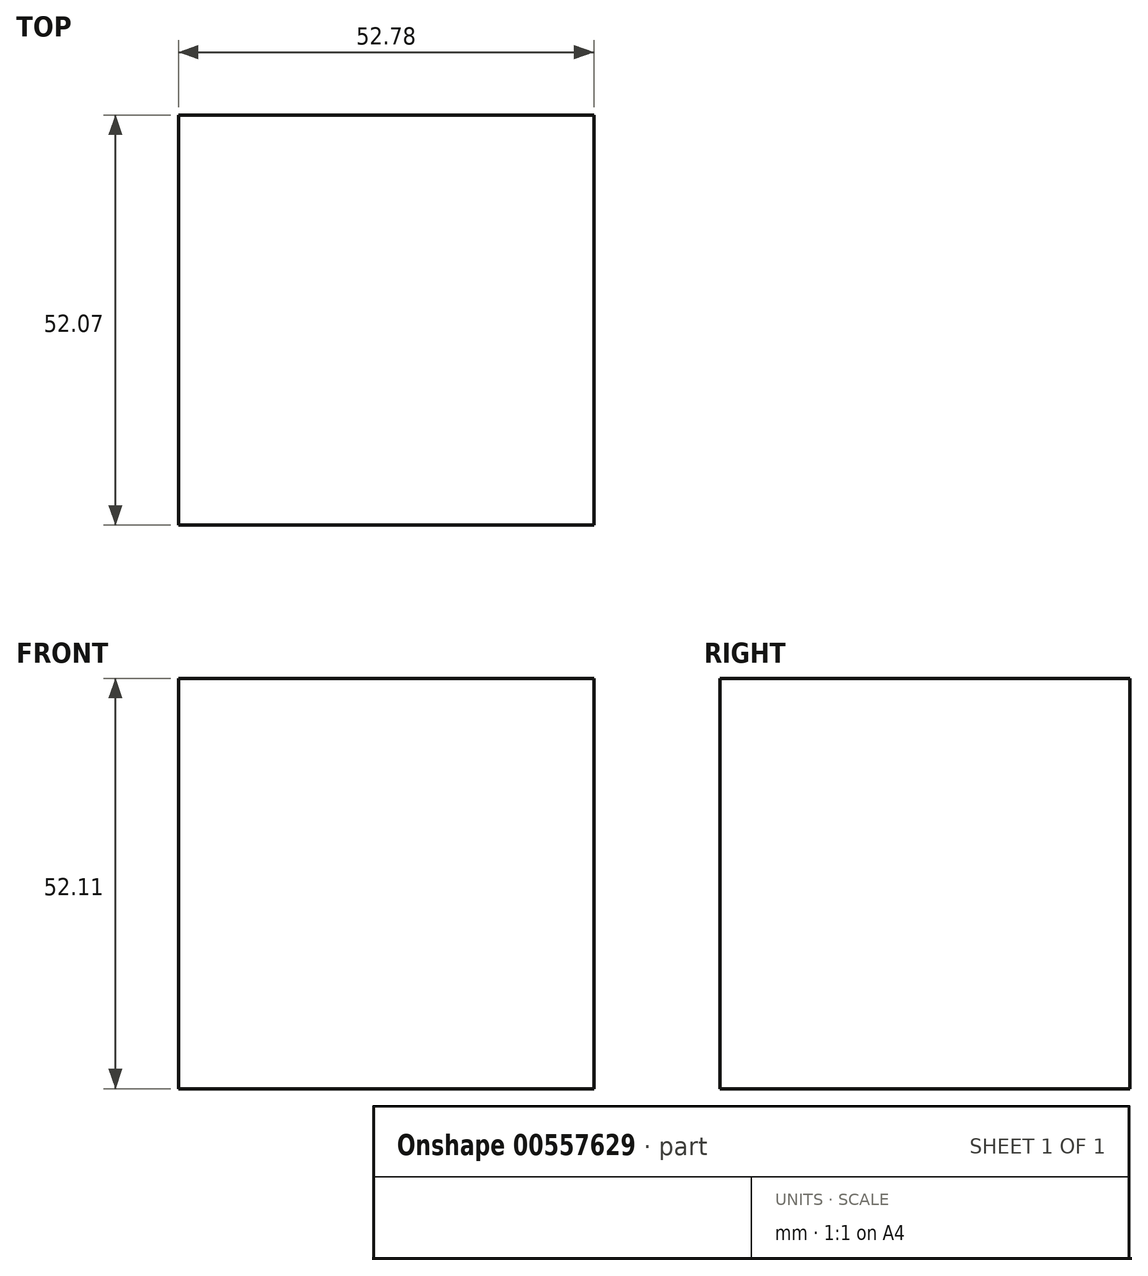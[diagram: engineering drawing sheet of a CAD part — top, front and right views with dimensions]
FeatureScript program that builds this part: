
annotation { "Feature Type Name" : "Feature", "Feature Type Description" : "" }
export const myFeature = defineFeature(function(context is Context, id is Id, definition is map)
    precondition{}
    {
        {
            var Q0;
            Q0=qCreatedBy(makeId("Front.planeOp"),FACE);
            var sketch = newSketch(context, id + "F0", { "sketchPlane" : qUnion([Q0])});
            skLineSegment(sketch, "E0.bottom", {"start": v(-21.84, 28.5) * mm, "end": v(30.94, 28.5) * mm});
            skLineSegment(sketch, "E0.top", {"start": v(-21.84, -23.6) * mm, "end": v(30.94, -23.6) * mm});
            skLineSegment(sketch, "E0.left", {"start": v(-21.84, 28.5) * mm, "end": v(-21.84, -23.6) * mm});
            skLineSegment(sketch, "E0.right", {"start": v(30.94, 28.5) * mm, "end": v(30.94, -23.6) * mm});
            skLineSegment(sketch, "E1.bottom", {"start": v(0, 0) * mm, "end": v(-12.29, 0) * mm});
            skLineSegment(sketch, "E1.top", {"start": v(0, -23.6) * mm, "end": v(-12.29, -23.6) * mm});
            skLineSegment(sketch, "E1.left", {"start": v(0, 0) * mm, "end": v(0, -23.6) * mm});
            skLineSegment(sketch, "E1.right", {"start": v(-12.29, 0) * mm, "end": v(-12.29, -23.6) * mm});
            skSolve(sketch);
        }
        {
            var Q0;
            Q0 = qSketchRegion(id + "F0", true);
            extrude(context, id + "F1", {"entities" : qUnion([Q0]), "depth" : 52.07 * mm, "offsetDistance" : 25.4 * mm});
        }
    });
